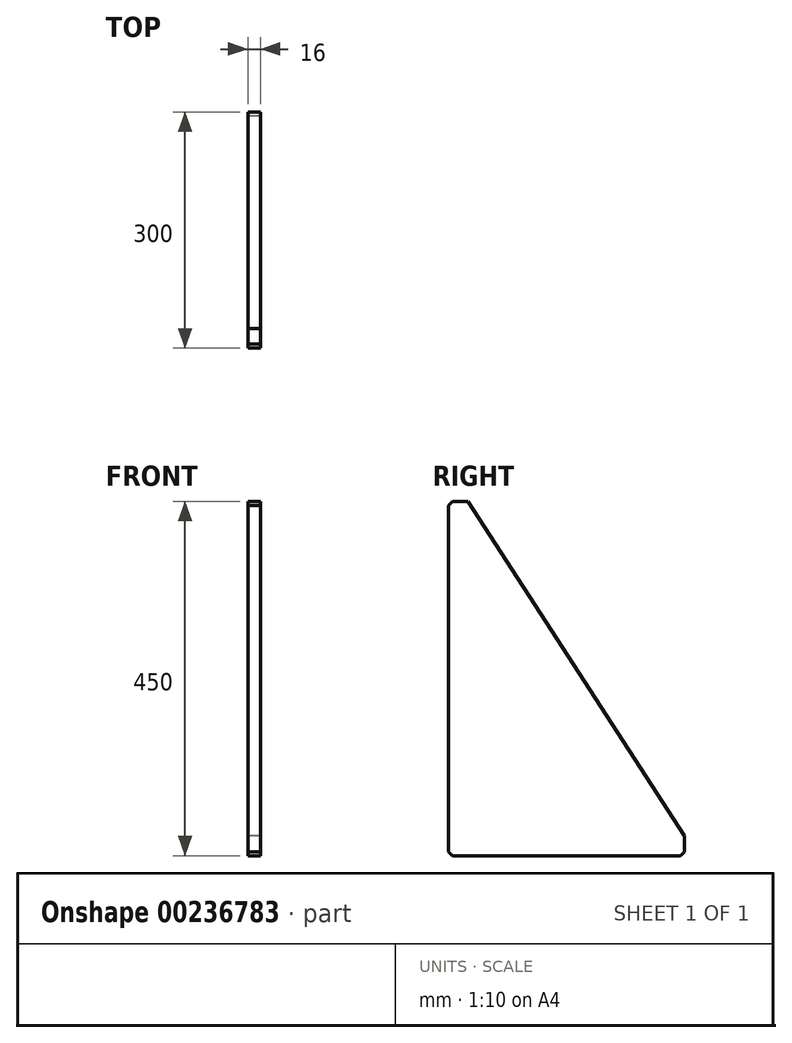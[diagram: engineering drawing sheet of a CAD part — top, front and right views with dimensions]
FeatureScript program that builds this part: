
annotation { "Feature Type Name" : "Feature", "Feature Type Description" : "" }
export const myFeature = defineFeature(function(context is Context, id is Id, definition is map)
    precondition{}
    {
        {
            var Q0;
            Q0=qCreatedBy(makeId("Right.planeOp"),FACE);
            var sketch = newSketch(context, id + "F0", { "sketchPlane" : qUnion([Q0])});
            skLineSegment(sketch, "E0.bottom", {"start": v(0, 0) * mm, "end": v(300, 0) * mm});
            skLineSegment(sketch, "E0.left", {"start": v(0, 0) * mm, "end": v(0, 450) * mm});
            skLineSegment(sketch, "E1", {"start": v(0, 450) * mm, "end": v(25, 450) * mm});
            skLineSegment(sketch, "E2", {"start": v(300, 0) * mm, "end": v(300, 25) * mm});
            skLineSegment(sketch, "E3", {"start": v(300, 25) * mm, "end": v(25, 450) * mm});
            skSolve(sketch);
        }
        {
            var Q0;
            Q0 = qSketchRegion(id + "F0", true);
            extrude(context, id + "F1", {"entities" : qUnion([Q0]), "flatOperationType" : FlatOperationType.REMOVE, "depth" : 16 * mm, "offsetDistance" : 25 * mm, "domain" : OperationDomain.MODEL});
        }
        {
            var Q0;
            Q0=makeQuery(id+"F1.opExtrude","SWEPT_EDGE",EDGE,{"disambiguationData":[OSD([sQuery(id+"F0.wireOp",EDGE,"E0.bottom"),sQuery(id+"F0.wireOp",EDGE,"04tgIPgq-DjGU-ceOV-5EwX-m6Nkmm3d1PjA")])]});
            var Q1;
            Q1=makeQuery(id+"F1.opExtrude","SWEPT_EDGE",EDGE,{"disambiguationData":[OSD([sQuery(id+"F0.wireOp",EDGE,"E0.left"),sQuery(id+"F0.wireOp",EDGE,"04tgIPgq-DjGU-ceOV-5EwX-m6Nkmm3d1PjA")])]});
            chamfer(context, id + "F2", {"entities" : qUnion([Q0, Q1]), "width" : 5 * mm, "tangentPropagation" : true});
        }
    });
